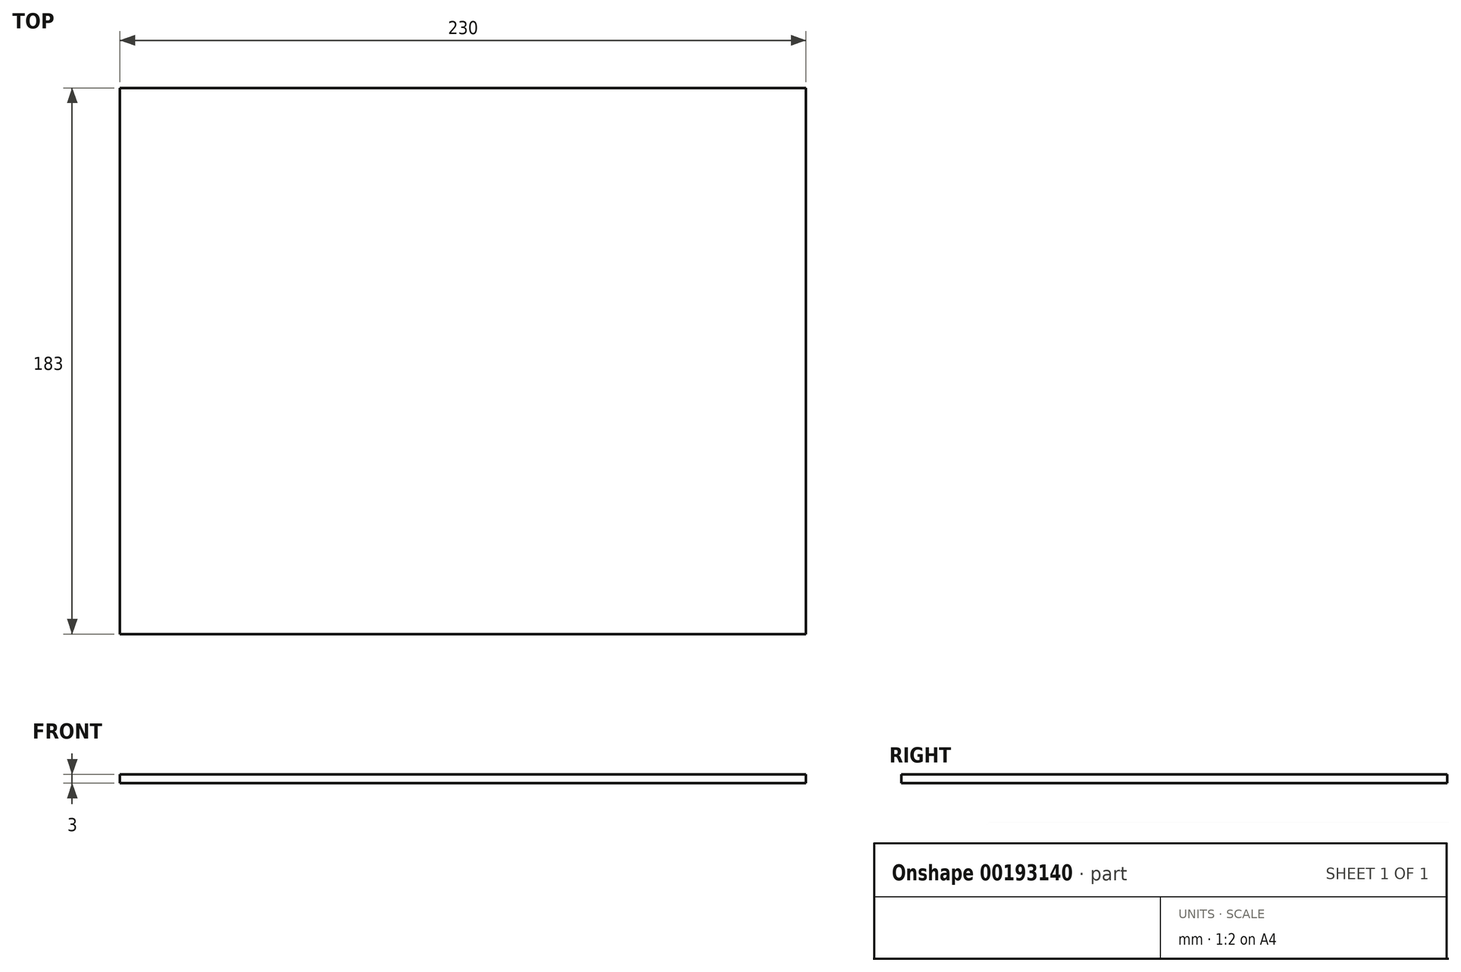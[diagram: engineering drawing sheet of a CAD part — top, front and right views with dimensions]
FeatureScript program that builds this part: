
annotation { "Feature Type Name" : "Feature", "Feature Type Description" : "" }
export const myFeature = defineFeature(function(context is Context, id is Id, definition is map)
    precondition{}
    {
        {
            var Q0;
            Q0=qCreatedBy(makeId("Top.planeOp"),FACE);
            var sketch = newSketch(context, id + "F0", { "sketchPlane" : qUnion([Q0])});
            skLineSegment(sketch, "E0.bottom", {"start": v(0, 0) * mm, "end": v(230, 0) * mm});
            skLineSegment(sketch, "E0.top", {"start": v(0, 183) * mm, "end": v(230, 183) * mm});
            skLineSegment(sketch, "E0.left", {"start": v(0, 0) * mm, "end": v(0, 183) * mm});
            skLineSegment(sketch, "E0.right", {"start": v(230, 0) * mm, "end": v(230, 183) * mm});
            skSolve(sketch);
        }
        {
            var Q0;
            Q0=makeQuery(id+"F0.imprint","IMPRINT",FACE,{"disambiguationData":[TD([[makeQuery(id+"F0.imprint","IMPRINT",EDGE,{"derivedFrom":sQuery(id+"F0.wireOp",EDGE,"E0.bottom")}),1.0]])]});
            extrude(context, id + "F1", {"entities" : qUnion([Q0]), "depth" : 3 * mm});
        }
    });
